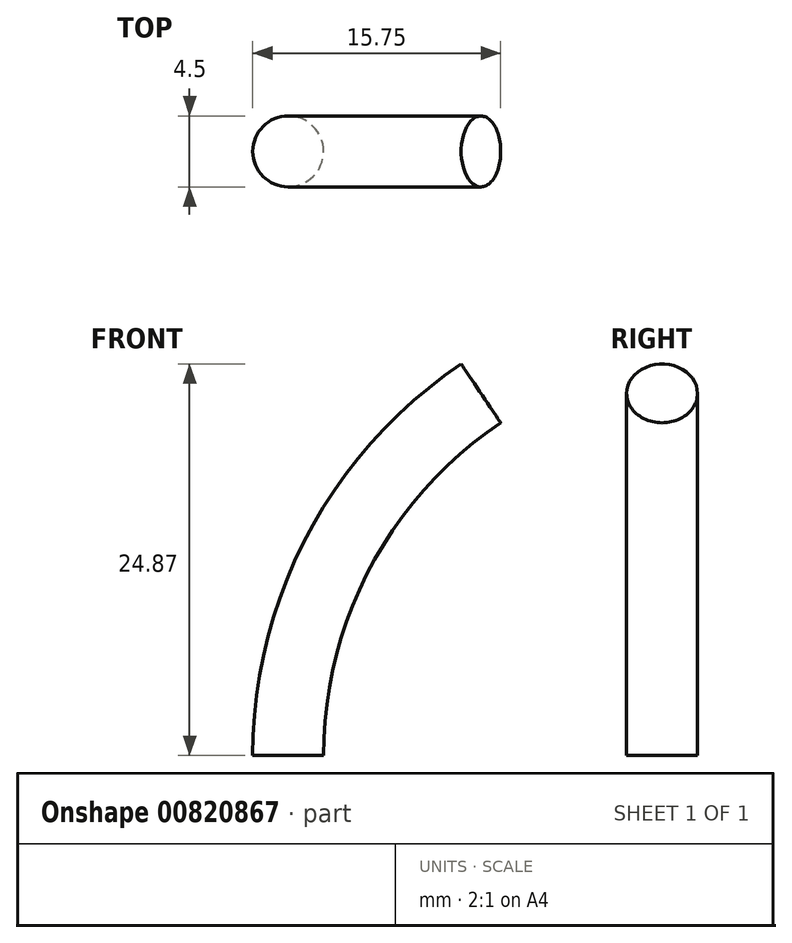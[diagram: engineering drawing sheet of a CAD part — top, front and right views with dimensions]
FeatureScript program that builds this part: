
annotation { "Feature Type Name" : "Feature", "Feature Type Description" : "" }
export const myFeature = defineFeature(function(context is Context, id is Id, definition is map)
    precondition{}
    {
        {
            var Q0;
            Q0=qCreatedBy(makeId("Top.planeOp"),FACE);
            var sketch = newSketch(context, id + "F0", { "sketchPlane" : qUnion([Q0])});
            skCircle(sketch, "E0", {"center": v(0, 0) * mm, "radius": 2.25 * mm});
            skSolve(sketch);
        }
        {
            var Q0;
            Q0=qCreatedBy(makeId("Front.planeOp"),FACE);
            var sketch = newSketch(context, id + "F1", { "sketchPlane" : qUnion([Q0])});
            skArc(sketch, "E1", {"start": v(12.24, 23) * mm, "mid": v(3.25, 13.03) * mm, "end": v(0, 0) * mm});
            skLineSegment(sketch, "E2", {"start": v(0, 0) * mm, "end": v(0, 33.96) * mm, "construction": true});
            skSolve(sketch);
        }
        {
            var Q0;
            Q0=makeQuery(id+"F0.imprint","IMPRINT",FACE,{"disambiguationData":[TD([[makeQuery(id+"F0.imprint","IMPRINT",EDGE,{"derivedFrom":sQuery(id+"F0.wireOp",EDGE,"E0")}),1.0]])]});
            var Q1;
            Q1=sQuery(id+"F1.wireOp",EDGE,"E1");
            sweep(context, id + "F2", {"profiles" : qUnion([Q0]), "path" : qUnion([Q1])});
        }
    });
